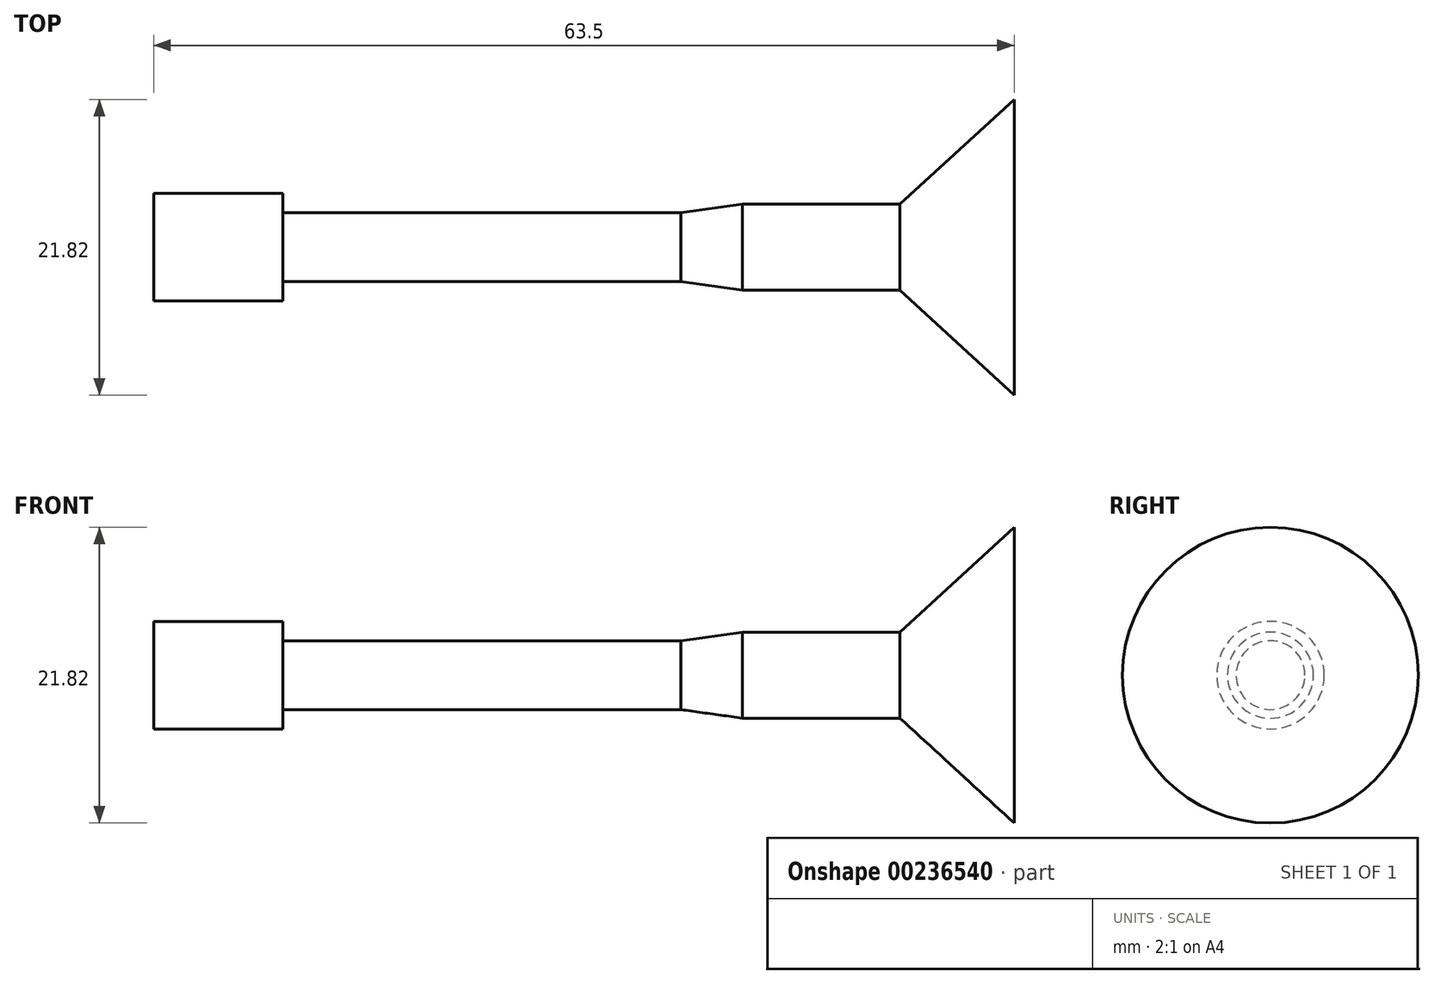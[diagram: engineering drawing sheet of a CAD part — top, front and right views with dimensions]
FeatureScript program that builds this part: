
annotation { "Feature Type Name" : "Feature", "Feature Type Description" : "" }
export const myFeature = defineFeature(function(context is Context, id is Id, definition is map)
    precondition{}
    {
        {
            var Q0;
            Q0=qCreatedBy(makeId("Front.planeOp"),FACE);
            var sketch = newSketch(context, id + "F0", { "sketchPlane" : qUnion([Q0])});
            skLineSegment(sketch, "E0", {"start": v(0, 0) * mm, "end": v(0, 3.97) * mm});
            skLineSegment(sketch, "E1", {"start": v(0, 3.97) * mm, "end": v(9.53, 3.97) * mm});
            skLineSegment(sketch, "E2", {"start": v(9.53, 3.97) * mm, "end": v(9.53, 2.54) * mm});
            skLineSegment(sketch, "E3", {"start": v(9.53, 2.54) * mm, "end": v(38.9, 2.54) * mm});
            skLineSegment(sketch, "E4", {"start": v(38.9, 2.54) * mm, "end": v(43.45, 3.18) * mm});
            skLineSegment(sketch, "E5", {"start": v(43.45, 3.18) * mm, "end": v(55.07, 3.18) * mm});
            skLineSegment(sketch, "E6", {"start": v(55.07, 3.18) * mm, "end": v(63.5, 10.91) * mm});
            skLineSegment(sketch, "E7", {"start": v(63.5, 10.91) * mm, "end": v(63.5, 0) * mm});
            skLineSegment(sketch, "E8", {"start": v(63.5, 0) * mm, "end": v(0, 0) * mm});
            skSolve(sketch);
        }
        {
            var Q0;
            Q0=makeQuery(id+"F0.imprint","IMPRINT",FACE,{"disambiguationData":[TD([[makeQuery(id+"F0.imprint","IMPRINT",EDGE,{"derivedFrom":sQuery(id+"F0.wireOp",EDGE,"E0")}),-1.0]])]});
            var Q1;
            Q1=sQuery(id+"F0.wireOp",EDGE,"E8");
            revolve(context, id + "F1", {"entities" : qUnion([Q0]), "axis" : qUnion([Q1]), "revolveType" : RevolveType.FULL});
        }
    });
